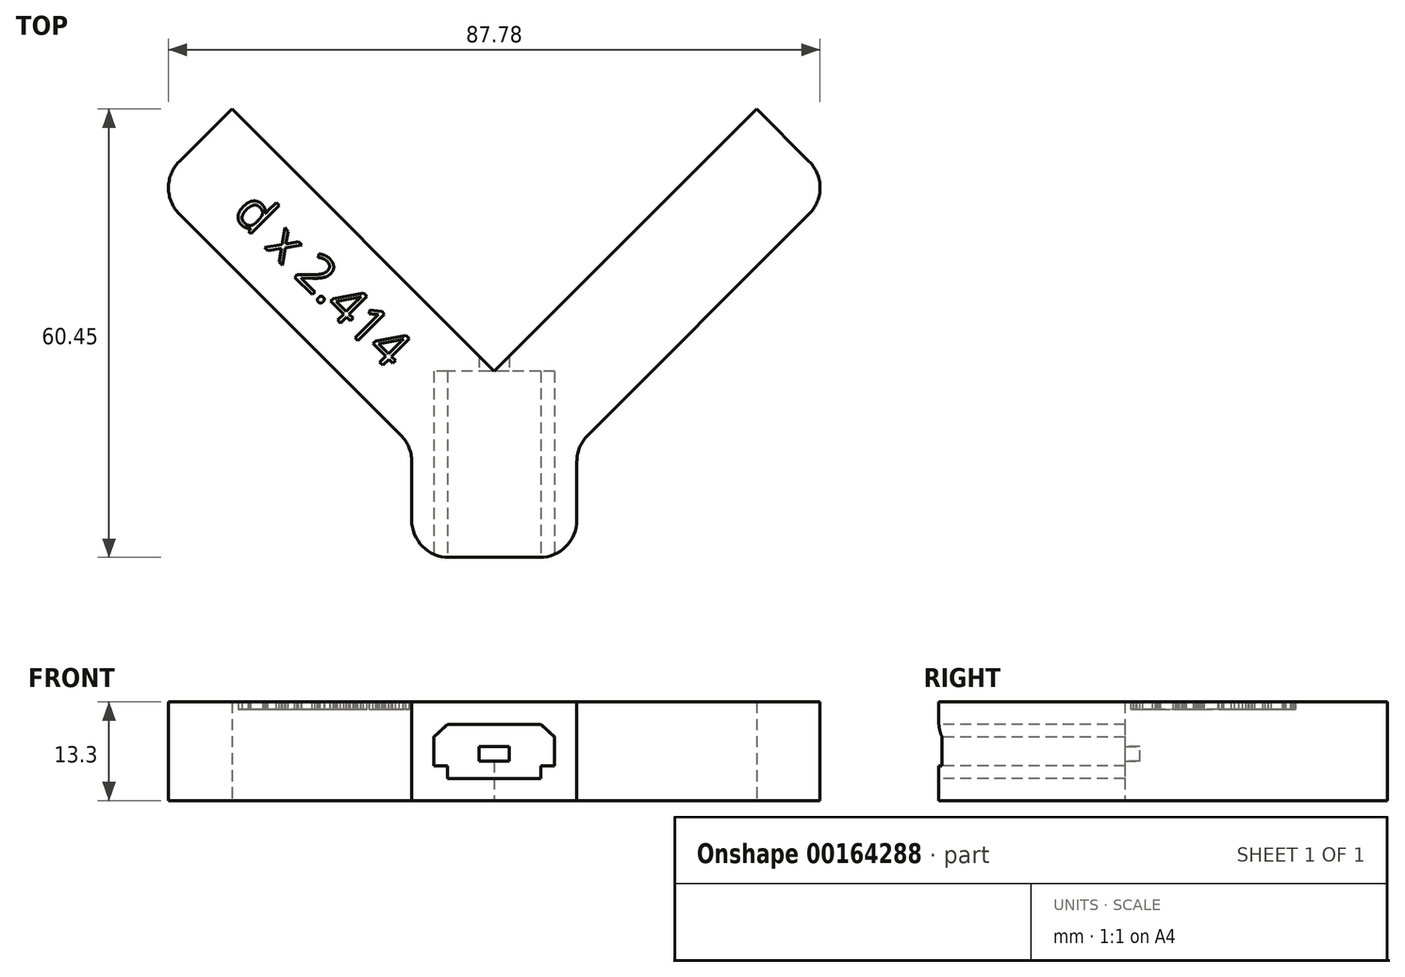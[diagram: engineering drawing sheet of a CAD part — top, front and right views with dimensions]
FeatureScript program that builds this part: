
annotation { "Feature Type Name" : "Feature", "Feature Type Description" : "" }
export const myFeature = defineFeature(function(context is Context, id is Id, definition is map)
    precondition{}
    {
        {
            var Q0;
            Q0=qCreatedBy(makeId("Top.planeOp"),FACE);
            var sketch = newSketch(context, id + "F0", { "sketchPlane" : qUnion([Q0])});
            skLineSegment(sketch, "E0", {"start": v(0, 0) * mm, "end": v(35.36, 35.36) * mm});
            skLineSegment(sketch, "E1", {"start": v(0, 0) * mm, "end": v(-35.36, 35.36) * mm});
            skLineSegment(sketch, "E2", {"start": v(0, 62.25) * mm, "end": v(0, -49.82) * mm, "construction": true});
            skLineSegment(sketch, "E3", {"start": v(35.36, 35.36) * mm, "end": v(42.43, 28.28) * mm});
            skLineSegment(sketch, "E4", {"start": v(42.43, 21.21) * mm, "end": v(12.59, -8.62) * mm});
            skLineSegment(sketch, "E5", {"start": v(11.13, -12.16) * mm, "end": v(11.12, -20.09) * mm});
            skLineSegment(sketch, "E6", {"start": v(6.12, -25.09) * mm, "end": v(-6.13, -25.09) * mm});
            skLineSegment(sketch, "E7", {"start": v(-11.12, -20.09) * mm, "end": v(-11.12, -12.16) * mm});
            skLineSegment(sketch, "E8", {"start": v(-12.59, -8.62) * mm, "end": v(-42.43, 21.21) * mm});
            skLineSegment(sketch, "E9", {"start": v(-42.43, 28.28) * mm, "end": v(-35.36, 35.36) * mm});
            skPoint(sketch, "E10.visualSharp", {"position": v(45.96, 24.75) * mm});
            skArc(sketch, "E10.filletArc", {"start": v(42.43, 21.21) * mm, "mid": v(43.9, 24.75) * mm, "end": v(42.43, 28.28) * mm});
            skPoint(sketch, "E11.visualSharp", {"position": v(-45.96, 24.75) * mm});
            skArc(sketch, "E11.filletArc", {"start": v(-42.43, 28.28) * mm, "mid": v(-43.9, 24.75) * mm, "end": v(-42.43, 21.21) * mm});
            skPoint(sketch, "E12.visualSharp", {"position": v(-11.12, -10.09) * mm});
            skArc(sketch, "E12.filletArc", {"start": v(-11.12, -12.16) * mm, "mid": v(-11.5, -10.25) * mm, "end": v(-12.59, -8.62) * mm});
            skPoint(sketch, "E13.visualSharp", {"position": v(11.13, -10.09) * mm});
            skArc(sketch, "E13.filletArc", {"start": v(12.59, -8.62) * mm, "mid": v(11.5, -10.25) * mm, "end": v(11.12, -12.16) * mm});
            skPoint(sketch, "E14.visualSharp", {"position": v(-11.13, -25.09) * mm});
            skArc(sketch, "E14.filletArc", {"start": v(-11.12, -20.09) * mm, "mid": v(-9.66, -23.62) * mm, "end": v(-6.13, -25.09) * mm});
            skPoint(sketch, "E15.visualSharp", {"position": v(11.12, -25.09) * mm});
            skArc(sketch, "E15.filletArc", {"start": v(6.12, -25.09) * mm, "mid": v(9.66, -23.62) * mm, "end": v(11.12, -20.09) * mm});
            skSolve(sketch);
        }
        {
            var Q0;
            Q0=makeQuery(id+"F0.imprint","IMPRINT",FACE,{"disambiguationData":[TD([[makeQuery(id+"F0.imprint","IMPRINT",EDGE,{"derivedFrom":sQuery(id+"F0.wireOp",EDGE,"E0")}),-1.0]])]});
            extrude(context, id + "F1", {"entities" : qUnion([Q0]), "depth" : (6.9 + 0.4 + 6) * mm});
        }
        {
            var Q0;
            Q0=makeQuery(id+"F1.opExtrude","SWEPT_FACE",FACE,{"disambiguationData":[OSD([sQuery(id+"F0.wireOp",EDGE,"E6")])]});
            var sketch = newSketch(context, id + "F2", { "sketchPlane" : qUnion([Q0])});
            skLineSegment(sketch, "E16", {"start": v(0, 13.3) * mm, "end": v(0, 0) * mm, "construction": true});
            skLineSegment(sketch, "E17", {"start": v(-6.12, 6.65) * mm, "end": v(6.13, 6.65) * mm, "construction": true});
            skLineSegment(sketch, "E18.top", {"start": v(8.13, 4.71) * mm, "end": v(-8.12, 4.71) * mm});
            skLineSegment(sketch, "E18.left", {"start": v(8.13, 8.6) * mm, "end": v(8.13, 4.7) * mm});
            skLineSegment(sketch, "E18.right", {"start": v(-8.12, 8.6) * mm, "end": v(-8.12, 4.71) * mm});
            skPoint(sketch, "E18.middle", {"position": v(0, 6.65) * mm});
            skLineSegment(sketch, "E19.bottom", {"start": v(6.28, 10.3) * mm, "end": v(-6.27, 10.3) * mm});
            skLineSegment(sketch, "E19.top", {"start": v(6.28, 3) * mm, "end": v(-6.27, 3) * mm});
            skLineSegment(sketch, "E19.left", {"start": v(6.28, 10.3) * mm, "end": v(6.28, 3) * mm});
            skLineSegment(sketch, "E19.right", {"start": v(-6.27, 10.3) * mm, "end": v(-6.27, 3) * mm});
            skLineSegment(sketch, "E20", {"start": v(-6.27, 10.3) * mm, "end": v(-8.12, 8.6) * mm});
            skLineSegment(sketch, "E21", {"start": v(6.28, 10.3) * mm, "end": v(8.13, 8.59) * mm});
            skSolve(sketch);
        }
        {
            var Q0;
            Q0 = qSketchRegion(id + "F2", true);
            var Q1;
            Q1=makeQuery(id+"F1.opExtrude","SWEPT_FACE",FACE,{"disambiguationData":[OSD([sQuery(id+"F0.wireOp",EDGE,"E0")])]});
            var Q2;
            Q2=makeQuery(id+"F1.opExtrude","SWEPT_BODY",BODY,{"disambiguationData":[OSD([sQuery(id+"F0.wireOp",EDGE,"E0"),sQuery(id+"F0.wireOp",EDGE,"E1"),sQuery(id+"F0.wireOp",EDGE,"E3"),sQuery(id+"F0.wireOp",EDGE,"E4"),sQuery(id+"F0.wireOp",EDGE,"E5"),sQuery(id+"F0.wireOp",EDGE,"E6"),sQuery(id+"F0.wireOp",EDGE,"E7"),sQuery(id+"F0.wireOp",EDGE,"E8"),sQuery(id+"F0.wireOp",EDGE,"E9"),sQuery(id+"F0.wireOp",EDGE,"E10.filletArc"),sQuery(id+"F0.wireOp",EDGE,"E11.filletArc"),sQuery(id+"F0.wireOp",EDGE,"E12.filletArc"),sQuery(id+"F0.wireOp",EDGE,"E13.filletArc"),sQuery(id+"F0.wireOp",EDGE,"E14.filletArc"),sQuery(id+"F0.wireOp",EDGE,"E15.filletArc")])]});
            extrude(context, id + "F3", {"entities" : qUnion([Q0]), "operationType" : NewBodyOperationType.REMOVE, "oppositeDirection" : true, "endBoundEntityFace" : qUnion([Q1]), "endBoundEntityBody" : qUnion([Q2]), "depth" : 25.09 * mm});
        }
        {
            var Q0;
            Q0=makeQuery(id+"F3.boolean.opBoolean","COPY",FACE,{"derivedFrom":makeQuery(id+"F3.opExtrude","CAP_FACE",FACE,{"disambiguationData":[OSD([sQuery(id+"F2.wireOp",EDGE,"E18.bottom"),sQuery(id+"F2.wireOp",EDGE,"E18.top"),sQuery(id+"F2.wireOp",EDGE,"E18.left"),sQuery(id+"F2.wireOp",EDGE,"E18.right"),sQuery(id+"F2.wireOp",EDGE,"E19.bottom"),sQuery(id+"F2.wireOp",EDGE,"E19.top"),sQuery(id+"F2.wireOp",EDGE,"E19.left"),sQuery(id+"F2.wireOp",EDGE,"E19.right")])],"isStart":false})});
            var sketch = newSketch(context, id + "F4", { "sketchPlane" : qUnion([Q0])});
            skLineSegment(sketch, "E22.bottom", {"start": v(2.02, 7.26) * mm, "end": v(-2.03, 7.26) * mm});
            skLineSegment(sketch, "E22.top", {"start": v(2.02, 5.31) * mm, "end": v(-2.03, 5.31) * mm});
            skLineSegment(sketch, "E22.left", {"start": v(2.02, 7.26) * mm, "end": v(2.02, 5.31) * mm});
            skLineSegment(sketch, "E22.right", {"start": v(-2.03, 7.26) * mm, "end": v(-2.03, 5.31) * mm});
            skPoint(sketch, "E22.middle", {"position": v(0, 6.29) * mm});
            skSolve(sketch);
        }
        {
            var Q0;
            Q0=makeQuery(id+"F4.imprint","IMPRINT",FACE,{"disambiguationData":[TD([[makeQuery(id+"F4.imprint","IMPRINT",EDGE,{"derivedFrom":sQuery(id+"F4.wireOp",EDGE,"E22.bottom")}),1.0]])]});
            extrude(context, id + "F5", {"entities" : qUnion([Q0]), "operationType" : NewBodyOperationType.REMOVE, "endBound" : BoundingType.THROUGH_ALL, "oppositeDirection" : true, "depth" : 25 * mm});
        }
        {
            var Q0;
            Q0=makeQuery(id+"F1.opExtrude","CAP_FACE",FACE,{"disambiguationData":[OSD([sQuery(id+"F0.wireOp",EDGE,"E0"),sQuery(id+"F0.wireOp",EDGE,"E1"),sQuery(id+"F0.wireOp",EDGE,"E3"),sQuery(id+"F0.wireOp",EDGE,"E4"),sQuery(id+"F0.wireOp",EDGE,"E5"),sQuery(id+"F0.wireOp",EDGE,"E6"),sQuery(id+"F0.wireOp",EDGE,"E7"),sQuery(id+"F0.wireOp",EDGE,"E8"),sQuery(id+"F0.wireOp",EDGE,"E9"),sQuery(id+"F0.wireOp",EDGE,"E10.filletArc"),sQuery(id+"F0.wireOp",EDGE,"E11.filletArc"),sQuery(id+"F0.wireOp",EDGE,"E12.filletArc"),sQuery(id+"F0.wireOp",EDGE,"E13.filletArc"),sQuery(id+"F0.wireOp",EDGE,"E14.filletArc"),sQuery(id+"F0.wireOp",EDGE,"E15.filletArc")])],"isStart":false});
            var sketch = newSketch(context, id + "F6", { "sketchPlane" : qUnion([Q0])});
            skText(sketch, "E23", { "text": "d x 2.414", "fontName": "OpenSans-Regular.ttf"});
            const initialGuessF6  = {"E23": [-0.0354, 0.02118, 0.7071, -0.7071, 0.00508]};
            skSetInitialGuess(sketch, initialGuessF6);
            skSolve(sketch);
        }
        {
            var Q0;
            Q0 = qSketchRegion(id + "F6", true);
            extrude(context, id + "F7", {"entities" : qUnion([Q0]), "operationType" : NewBodyOperationType.REMOVE, "oppositeDirection" : true, "depth" : 1 * mm});
        }
    });
